# Revit family: Electronics_Visual-Projectors_ViewSonic_The-ViewSonicR-LS800WU-Projector
name_source: partatom
category: Electrical Equipment
revit_build: Autodesk Revit 2015 (Build: 20140606_1530(x64)
units: mm (PartAtom-declared; Revit-internal decimal feet)

## types (1)
- LS800WU
    Assembly Code = D50
    BIMobject category = Visual - Projectors
    BIMobject category code = electronics-visual-projectors
    BIMobject main category = Electronics
    BIMobject main category code = electronics
    BOSUseNativeGeometries = 1
    Brand url = https://www.viewsonic.com
    Color (front face) = Viewsonic - Plastic - Black
    Covering Color = Plastic - Viewsonic - White
    Description = Bright and versatile for any professional installation, the ViewSonic® LS800WU WUXGA laser projector delivers everything you need for big screens in big venues. Delivering 5,500 lumens of advanced high brightness, 100,000:1 contrast ratio, and up to 30,000 hours* of light source life, this projector is ideal for auditoriums, lecture halls, large boardrooms, houses of worship, and more. Thanks to SuperColor™ technology, content is brought to life with captivating color, crisp graphics, and stunning videos no matter the environment. This top-notch performer is also easy to deploy and manage with its wide 1.65x optical zoom adjustment, vertical/horizontal keystone, 4 corner adjustment, and a vertical/horizontal lens shift feature that provide extreme flexibility in even the most challenging installations. Thanks to the built-in HDBT receiver, the projector is capable of receiving uncompressed HD video and audio from over 200 feet away via network cable. Moreover, 360-degree tilt angle projection, portrait mode, and 24/7 operation allow for extreme mounting flexibility. The ViewSonic® LS800WU is the ideal WUXGA laser projector for professional installations, large venues, and business and education environments.
    Design country = Taiwan
    Edition number = 1
    Keynote = V90
    Manufacturer = ViewSonic
    Manufacturer country = Taiwan
    Manufacturer name = ViewSonic
    Model = viewsonic_ls800WU
    Product Guid = 63a5f6ee-9a42-420b-938a-3a57af3ab72d
    Product SKU = viewsonic_ls800wu
    Product data url = https://bimobject.com
    Product family = Electronics
    Product group = Projectors
    Product name = The ViewSonic® LS800WU Projector
    Product url = https://www.viewsonic.com
    QR code = http://bimobject.com
    URL = www.viewsonic.com
    a = Image Aspect Ratio : "4  - 3"
    b = Image Aspect Ratio : "16 - 9"
    c = Image Aspect Ratio : "16 - 10"

## geometry (parser evidence)
native form markers: Blend x2, Sweep x10
no freeform markers — native parametric forms only
